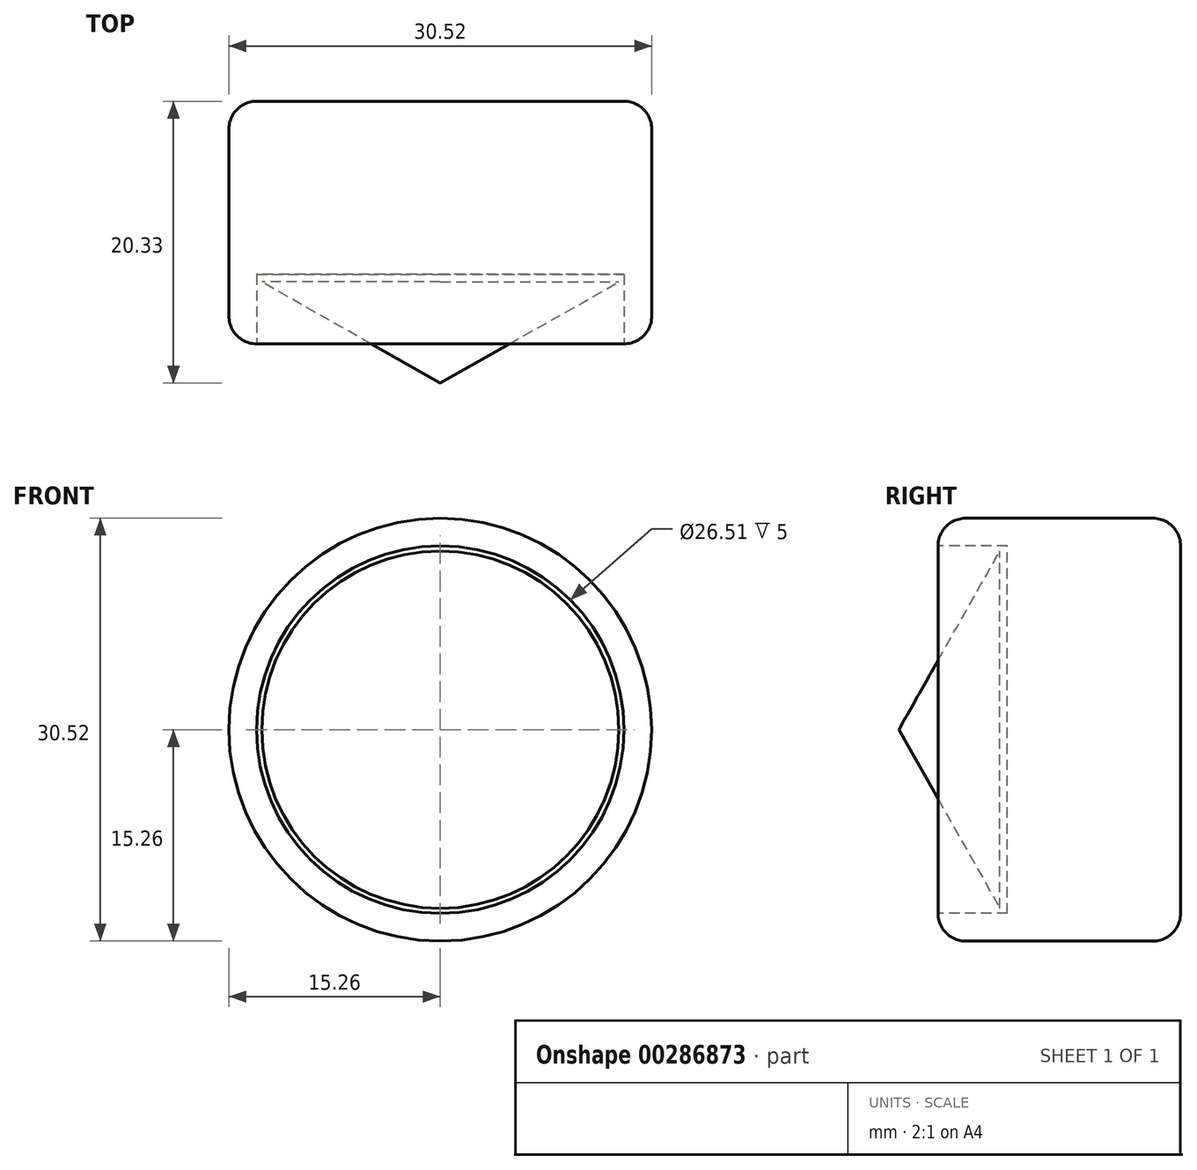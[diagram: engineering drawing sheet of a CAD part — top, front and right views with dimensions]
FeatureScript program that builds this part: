
annotation { "Feature Type Name" : "Feature", "Feature Type Description" : "" }
export const myFeature = defineFeature(function(context is Context, id is Id, definition is map)
    precondition{}
    {
        {
            var Q0;
            Q0=qCreatedBy(makeId("Front.planeOp"),FACE);
            var sketch = newSketch(context, id + "F0", { "sketchPlane" : qUnion([Q0])});
            skCircle(sketch, "E0", {"center": v(0, 0) * mm, "radius": 15.26 * mm});
            skSolve(sketch);
        }
        {
            var Q0;
            Q0 = qSketchRegion(id + "F0", true);
            extrude(context, id + "F1", {"entities" : qUnion([Q0]), "depth" : 17.5 * mm});
        }
        {
            var Q0;
            Q0=makeQuery(id+"F1.opExtrude","CAP_EDGE",EDGE,{"disambiguationData":[OSD([sQuery(id+"F0.wireOp",EDGE,"E0")])],"isStart":false});
            var Q1;
            Q1=makeQuery(id+"F1.opExtrude","CAP_EDGE",EDGE,{"disambiguationData":[OSD([sQuery(id+"F0.wireOp",EDGE,"E0")])],"isStart":true});
            fillet(context, id + "F2", {"entities" : qUnion([Q0, Q1]), "radius" : 2 * mm, "tangentPropagation" : true, "allowEdgeOverflow" : false});
        }
        {
            var Q0;
            Q0=makeQuery(id+"F1.opExtrude","CAP_FACE",FACE,{"disambiguationData":[OSD([sQuery(id+"F0.wireOp",EDGE,"E0")])],"isStart":false});
            extrude(context, id + "F3", {"entities" : qUnion([Q0]), "operationType" : NewBodyOperationType.REMOVE, "oppositeDirection" : true, "depth" : 5 * mm});
        }
        {
            var Q0;
            Q0=makeQuery(id+"F3.boolean.opBoolean","COPY",FACE,{"derivedFrom":makeQuery(id+"F3.opExtrude","CAP_FACE",FACE,{"disambiguationData":[OSD([sQuery(id+"F0.wireOp",EDGE,"E0")])],"isStart":false})});
            var sketch = newSketch(context, id + "F4", { "sketchPlane" : qUnion([Q0])});
            skSolve(sketch);
        }
        {
            var Q0;
            Q0=qCreatedBy(makeId("Right.planeOp"),FACE);
            var sketch = newSketch(context, id + "F5", { "sketchPlane" : qUnion([Q0])});
            skLineSegment(sketch, "E1", {"start": v(-13.04, 0) * mm, "end": v(-13.04, -12.89) * mm});
            skLineSegment(sketch, "E2", {"start": v(-13.04, -12.89) * mm, "end": v(-20.33, 0) * mm});
            skLineSegment(sketch, "E3", {"start": v(-20.33, 0) * mm, "end": v(-13.04, 0) * mm});
            skSolve(sketch);
        }
        {
            var Q0;
            Q0 = qSketchRegion(id + "F5", true);
            var Q1;
            Q1=sQuery(id+"F5.wireOp",EDGE,"E3");
            revolve(context, id + "F6", {"operationType" : NewBodyOperationType.ADD, "entities" : qUnion([Q0]), "axis" : qUnion([Q1]), "revolveType" : RevolveType.FULL});
        }
    });
